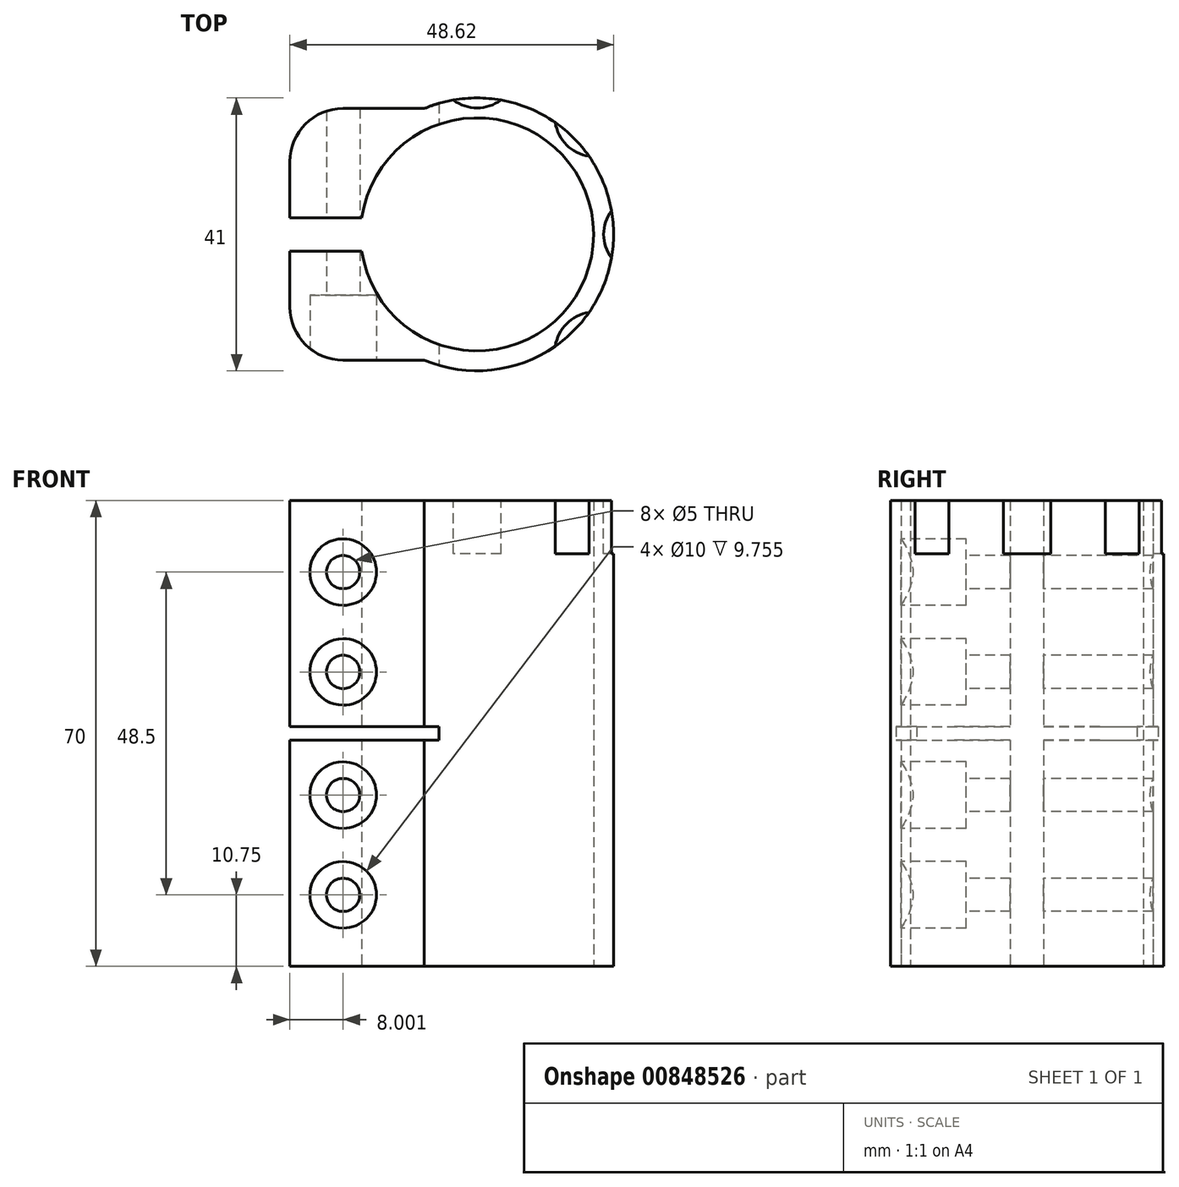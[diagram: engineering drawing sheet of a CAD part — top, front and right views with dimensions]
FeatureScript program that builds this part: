
annotation { "Feature Type Name" : "Feature", "Feature Type Description" : "" }
export const myFeature = defineFeature(function(context is Context, id is Id, definition is map)
    precondition{}
    {
        {
            var Q0;
            Q0=qCreatedBy(makeId("Top.planeOp"),FACE);
            var sketch = newSketch(context, id + "F0", { "sketchPlane" : qUnion([Q0])});
            skArc(sketch, "E0", {"start": v(-17.32, -2.5) * mm, "mid": v(17.5, 0) * mm, "end": v(-17.32, 2.5) * mm});
            skLineSegment(sketch, "E1", {"start": v(-17.32, 2.5) * mm, "end": v(-28.12, 2.5) * mm});
            skLineSegment(sketch, "E2", {"start": v(-7.92, 18.9) * mm, "end": v(-20.12, 18.9) * mm});
            skLineSegment(sketch, "E3", {"start": v(-28.12, 10.9) * mm, "end": v(-28.12, 2.5) * mm});
            skPoint(sketch, "E4.visualSharp", {"position": v(-28.12, 18.9) * mm});
            skArc(sketch, "E4.filletArc", {"start": v(-20.12, 18.9) * mm, "mid": v(-25.78, 16.57) * mm, "end": v(-28.12, 10.9) * mm});
            skLineSegment(sketch, "E5", {"start": v(0, 0) * mm, "end": v(48.84, 0) * mm, "construction": true});
            skLineSegment(sketch, "E6.MirrorCS", {"start": v(-7.92, -18.9) * mm, "end": v(-20.12, -18.9) * mm});
            skArc(sketch, "E7.MirrorCS", {"start": v(-20.12, -18.9) * mm, "mid": v(-25.78, -16.57) * mm, "end": v(-28.12, -10.9) * mm});
            skLineSegment(sketch, "E8.MirrorCS", {"start": v(-28.12, -10.9) * mm, "end": v(-28.12, -2.5) * mm});
            skLineSegment(sketch, "E9.MirrorCS", {"start": v(-17.32, -2.5) * mm, "end": v(-28.12, -2.5) * mm});
            skArc(sketch, "E10.trimOffspring", {"start": v(-7.92, -18.9) * mm, "mid": v(20.5, 0) * mm, "end": v(-7.92, 18.9) * mm});
            skSolve(sketch);
        }
        {
            var Q0;
            Q0=makeQuery(id+"F0.imprint","IMPRINT",FACE,{"disambiguationData":[TD([[makeQuery(id+"F0.imprint","IMPRINT",EDGE,{"derivedFrom":sQuery(id+"F0.wireOp",EDGE,"E0")}),-1.0]])]});
            extrude(context, id + "F1", {"entities" : qUnion([Q0]), "endBound" : BoundingType.SYMMETRIC, "depth" : 70 * mm, "offsetDistance" : 25 * mm});
        }
        {
            var Q0;
            Q0=makeQuery(id+"F1.opExtrude","SWEPT_FACE",FACE,{"disambiguationData":[OSD([sQuery(id+"F0.wireOp",EDGE,"E6.MirrorCS")])]});
            var sketch = newSketch(context, id + "F2", { "sketchPlane" : qUnion([Q0])});
            skPoint(sketch, "E11", {"position": v(-20.12, 24.25) * mm});
            skPoint(sketch, "E12", {"position": v(-20.12, 9.25) * mm});
            skPoint(sketch, "E13", {"position": v(-20.12, -9.25) * mm});
            skPoint(sketch, "E14", {"position": v(-20.12, -24.25) * mm});
            skSolve(sketch);
        }
        {
            var Q0;
            Q0=sQuery(id+"F2.wireOp",VERTEX,"E11");
            var Q1;
            Q1=sQuery(id+"F2.wireOp",VERTEX,"E12");
            var Q2;
            Q2=sQuery(id+"F2.wireOp",VERTEX,"E13");
            var Q3;
            Q3=sQuery(id+"F2.wireOp",VERTEX,"E14");
            var Q4;
            Q4=makeQuery(id+"F1.opExtrude","SWEPT_BODY",BODY,{"disambiguationData":[OSD([sQuery(id+"F0.wireOp",EDGE,"E0"),sQuery(id+"F0.wireOp",EDGE,"E1"),sQuery(id+"F0.wireOp",EDGE,"E2"),sQuery(id+"F0.wireOp",EDGE,"E3"),sQuery(id+"F0.wireOp",EDGE,"E4.filletArc"),sQuery(id+"F0.wireOp",EDGE,"E6.MirrorCS"),sQuery(id+"F0.wireOp",EDGE,"E7.MirrorCS"),sQuery(id+"F0.wireOp",EDGE,"E8.MirrorCS"),sQuery(id+"F0.wireOp",EDGE,"E9.MirrorCS"),sQuery(id+"F0.wireOp",EDGE,"E10.trimOffspring")])]});
            hole(context, id + "F3", {"style" : HoleStyle.C_BORE, "endStyle" : HoleEndStyle.THROUGH, "holeDiameter" : 5 * mm, "cBoreDiameter" : 10 * mm, "cBoreDepth" : 8 * mm, "majorDiameter" : 5 * mm, "isTappedThrough" : true, "tappedDepth" : 12 * mm, "tapClearance" : 3, "locations" : qUnion([Q0, Q1, Q2, Q3]), "scope" : qUnion([Q4])});
        }
        {
            var Q0;
            Q0=qCreatedBy(makeId("Front.planeOp"),FACE);
            var sketch = newSketch(context, id + "F4", { "sketchPlane" : qUnion([Q0])});
            skLineSegment(sketch, "E15.bottom", {"start": v(-28.12, 1) * mm, "end": v(-5.72, 1) * mm});
            skLineSegment(sketch, "E15.top", {"start": v(-28.12, -1) * mm, "end": v(-5.72, -1) * mm});
            skLineSegment(sketch, "E15.left", {"start": v(-28.12, 1) * mm, "end": v(-28.12, -1) * mm});
            skLineSegment(sketch, "E15.right", {"start": v(-5.72, 1) * mm, "end": v(-5.72, -1) * mm});
            skSolve(sketch);
        }
        {
            var Q0;
            Q0=makeQuery(id+"F4.imprint","IMPRINT",FACE,{"disambiguationData":[TD([[makeQuery(id+"F4.imprint","IMPRINT",EDGE,{"derivedFrom":sQuery(id+"F4.wireOp",EDGE,"E15.bottom")}),-1.0]])]});
            extrude(context, id + "F5", {"entities" : qUnion([Q0]), "operationType" : NewBodyOperationType.REMOVE, "endBound" : BoundingType.SYMMETRIC, "oppositeDirection" : true, "depth" : 50 * mm, "offsetDistance" : 25 * mm});
        }
        {
            var Q0;
            Q0=makeQuery(id+"F1.opExtrude","CAP_FACE",FACE,{"disambiguationData":[OSD([sQuery(id+"F0.wireOp",EDGE,"E0"),sQuery(id+"F0.wireOp",EDGE,"E1"),sQuery(id+"F0.wireOp",EDGE,"E2"),sQuery(id+"F0.wireOp",EDGE,"E3"),sQuery(id+"F0.wireOp",EDGE,"E4.filletArc"),sQuery(id+"F0.wireOp",EDGE,"E6.MirrorCS"),sQuery(id+"F0.wireOp",EDGE,"E7.MirrorCS"),sQuery(id+"F0.wireOp",EDGE,"E8.MirrorCS"),sQuery(id+"F0.wireOp",EDGE,"E9.MirrorCS"),sQuery(id+"F0.wireOp",EDGE,"E10.trimOffspring")])],"isStart":false});
            var sketch = newSketch(context, id + "F6", { "sketchPlane" : qUnion([Q0])});
            skCircle(sketch, "E16", {"center": v(0, -25) * mm, "radius": 6 * mm});
            skCircle(sketch, "E17.1.0", {"center": v(17.68, -17.68) * mm, "radius": 6 * mm});
            skCircle(sketch, "E17.2.0", {"center": v(25, 0) * mm, "radius": 6 * mm});
            skCircle(sketch, "E17.3.0", {"center": v(17.68, 17.68) * mm, "radius": 6 * mm});
            skCircle(sketch, "E17.4.0", {"center": v(0, 25) * mm, "radius": 6 * mm});
            skPoint(sketch, "E17.center", {"position": v(0, 0) * mm});
            skLineSegment(sketch, "E17.anchor1", {"start": v(0, 0) * mm, "end": v(0, -25) * mm, "construction": true});
            skLineSegment(sketch, "E17.anchor2", {"start": v(0, 0) * mm, "end": v(0, 25) * mm, "construction": true});
            skSolve(sketch);
        }
        {
            var Q0;
            {var subQ0=sQuery(id+"F6.wireOp",EDGE,"E17.4.0");var subQ1=makeQuery(id+"F1.opExtrude","CAP_EDGE",EDGE,{"disambiguationData":[OSD([sQuery(id+"F0.wireOp",EDGE,"E10.trimOffspring")])],"isStart":false});var subQ2=makeQuery(id+"F6.imprint","INTERSECT",VERTEX,{"disambiguationData":[OD(0.0)],"derivedFrom":[subQ1,subQ0]});Q0=makeQuery(id+"F6.imprint","IMPRINT",FACE,{"disambiguationData":[TD([[makeQuery(id+"F6.imprint","IMPRINT",EDGE,{"disambiguationData":[TD([[subQ2,1.0]])],"derivedFrom":subQ0}),1.0]])]});}
            var Q1;
            {var subQ0=sQuery(id+"F6.wireOp",EDGE,"E17.3.0");var subQ1=makeQuery(id+"F1.opExtrude","CAP_EDGE",EDGE,{"disambiguationData":[OSD([sQuery(id+"F0.wireOp",EDGE,"E10.trimOffspring")])],"isStart":false});var subQ2=makeQuery(id+"F6.imprint","INTERSECT",VERTEX,{"disambiguationData":[OD(0.0)],"derivedFrom":[subQ1,subQ0]});Q1=makeQuery(id+"F6.imprint","IMPRINT",FACE,{"disambiguationData":[TD([[makeQuery(id+"F6.imprint","IMPRINT",EDGE,{"disambiguationData":[TD([[subQ2,1.0]])],"derivedFrom":subQ0}),1.0]])]});}
            var Q2;
            {var subQ0=sQuery(id+"F6.wireOp",EDGE,"E16");var subQ1=makeQuery(id+"F1.opExtrude","CAP_EDGE",EDGE,{"disambiguationData":[OSD([sQuery(id+"F0.wireOp",EDGE,"E10.trimOffspring")])],"isStart":false});var subQ2=makeQuery(id+"F6.imprint","INTERSECT",VERTEX,{"disambiguationData":[OD(0.0)],"derivedFrom":[subQ1,subQ0]});Q2=makeQuery(id+"F6.imprint","IMPRINT",FACE,{"disambiguationData":[TD([[makeQuery(id+"F6.imprint","IMPRINT",EDGE,{"disambiguationData":[TD([[subQ2,-1.0]])],"derivedFrom":subQ0}),1.0]])]});}
            var Q3;
            {var subQ0=sQuery(id+"F6.wireOp",EDGE,"E17.2.0");var subQ1=makeQuery(id+"F1.opExtrude","CAP_EDGE",EDGE,{"disambiguationData":[OSD([sQuery(id+"F0.wireOp",EDGE,"E10.trimOffspring")])],"isStart":false});var subQ2=makeQuery(id+"F6.imprint","INTERSECT",VERTEX,{"disambiguationData":[OD(0.0)],"derivedFrom":[subQ1,subQ0]});Q3=makeQuery(id+"F6.imprint","IMPRINT",FACE,{"disambiguationData":[TD([[makeQuery(id+"F6.imprint","IMPRINT",EDGE,{"disambiguationData":[TD([[subQ2,-1.0]])],"derivedFrom":subQ0}),1.0]])]});}
            var Q4;
            {var subQ0=sQuery(id+"F6.wireOp",EDGE,"E17.1.0");var subQ1=makeQuery(id+"F1.opExtrude","CAP_EDGE",EDGE,{"disambiguationData":[OSD([sQuery(id+"F0.wireOp",EDGE,"E10.trimOffspring")])],"isStart":false});var subQ2=makeQuery(id+"F6.imprint","INTERSECT",VERTEX,{"disambiguationData":[OD(0.0)],"derivedFrom":[subQ1,subQ0]});Q4=makeQuery(id+"F6.imprint","IMPRINT",FACE,{"disambiguationData":[TD([[makeQuery(id+"F6.imprint","IMPRINT",EDGE,{"disambiguationData":[TD([[subQ2,-1.0]])],"derivedFrom":subQ0}),1.0]])]});}
            var Q5;
            {var subQ0=sQuery(id+"F6.wireOp",EDGE,"E17.3.0");var subQ1=makeQuery(id+"F1.opExtrude","CAP_EDGE",EDGE,{"disambiguationData":[OSD([sQuery(id+"F0.wireOp",EDGE,"E10.trimOffspring")])],"isStart":false});var subQ2=makeQuery(id+"F6.imprint","INTERSECT",VERTEX,{"disambiguationData":[OD(0.0)],"derivedFrom":[subQ1,subQ0]});Q5=makeQuery(id+"F6.imprint","IMPRINT",FACE,{"disambiguationData":[TD([[makeQuery(id+"F6.imprint","IMPRINT",EDGE,{"disambiguationData":[TD([[subQ2,-1.0]])],"derivedFrom":subQ0}),1.0]])]});}
            var Q6;
            {var subQ0=sQuery(id+"F6.wireOp",EDGE,"E17.4.0");var subQ1=makeQuery(id+"F1.opExtrude","CAP_EDGE",EDGE,{"disambiguationData":[OSD([sQuery(id+"F0.wireOp",EDGE,"E10.trimOffspring")])],"isStart":false});var subQ2=makeQuery(id+"F6.imprint","INTERSECT",VERTEX,{"disambiguationData":[OD(0.0)],"derivedFrom":[subQ1,subQ0]});Q6=makeQuery(id+"F6.imprint","IMPRINT",FACE,{"disambiguationData":[TD([[makeQuery(id+"F6.imprint","IMPRINT",EDGE,{"disambiguationData":[TD([[subQ2,-1.0]])],"derivedFrom":subQ0}),1.0]])]});}
            var Q7;
            {var subQ0=sQuery(id+"F6.wireOp",EDGE,"E17.2.0");var subQ1=makeQuery(id+"F1.opExtrude","CAP_EDGE",EDGE,{"disambiguationData":[OSD([sQuery(id+"F0.wireOp",EDGE,"E10.trimOffspring")])],"isStart":false});var subQ2=makeQuery(id+"F6.imprint","INTERSECT",VERTEX,{"disambiguationData":[OD(0.0)],"derivedFrom":[subQ1,subQ0]});Q7=makeQuery(id+"F6.imprint","IMPRINT",FACE,{"disambiguationData":[TD([[makeQuery(id+"F6.imprint","IMPRINT",EDGE,{"disambiguationData":[TD([[subQ2,1.0]])],"derivedFrom":subQ0}),1.0]])]});}
            var Q8;
            {var subQ0=sQuery(id+"F6.wireOp",EDGE,"E17.1.0");var subQ1=makeQuery(id+"F1.opExtrude","CAP_EDGE",EDGE,{"disambiguationData":[OSD([sQuery(id+"F0.wireOp",EDGE,"E10.trimOffspring")])],"isStart":false});var subQ2=makeQuery(id+"F6.imprint","INTERSECT",VERTEX,{"disambiguationData":[OD(0.0)],"derivedFrom":[subQ1,subQ0]});Q8=makeQuery(id+"F6.imprint","IMPRINT",FACE,{"disambiguationData":[TD([[makeQuery(id+"F6.imprint","IMPRINT",EDGE,{"disambiguationData":[TD([[subQ2,1.0]])],"derivedFrom":subQ0}),1.0]])]});}
            extrude(context, id + "F7", {"entities" : qUnion([Q0, Q1, Q2, Q3, Q4, Q5, Q6, Q7, Q8]), "operationType" : NewBodyOperationType.REMOVE, "oppositeDirection" : true, "depth" : 8 * mm, "offsetDistance" : 25 * mm});
        }
    });
